# Revit family: P190780JX-138c_JIE4115GS_Black-StainlessSteelTrim_JA_Cooking_Cooktops
name_source: partatom
category: Specialty Equipment
units: mm (PartAtom-declared; Revit-internal decimal feet)

## family parameters
Always vertical = Yes
Cut with Voids When Loaded = No
Enable Cutting in Views = No
Maintain Annotation Orientation = No
Part Type = Normal
Room Calculation Point = No
Round Connector Dimension = Use Diameter
Shared = No
Work Plane-Based = No

## types (1)
- JIE4115GS
    Amps = 20 A
    Body Material = ARCAT - Metal - Steel - Stainless
    Cooktop Edge Material = ARCAT - Metal - Steel - Stainless
    Cooktop Material = ARCAT - Glass - Black
    Default Elevation = 0"
    Depth = 21"
    Description = Custom 15" Induction Wok
Table de cuisson modulaire à induction pour wok de 15 po
    Dimension Guide = http://access.whirlpool.com Guide&sku=JIE4115GS&language=EN
http://access.whirlpool.com Guide&sku=JIE4115GS&language=EN
    Family Name = INDUCTION UPDRAFT COOKTOP - 15"
    Feature 1 = Induction Technology
Technologie à induction
    Feature 2 = Induction Wok Element
Élément pour wok à induction
    Feature 3 = Glass-Touch Electronic Controls
Commandes électroniques à effleurement sous verre
    Height = 1/8"
    Installation-Fabrication = http://access.whirlpool.com Instruction&sku=JIE4115GS&language=EN
http://access.whirlpool.com Instruction&sku=JIE4115GS&language=FR
    Manufacturer = Jenn Air
    Model = JIE4115GS
    Voltage = 0 V
    Width = 15"

## geometry (parser evidence)
native form markers: Sweep x3
no freeform markers — native parametric forms only
